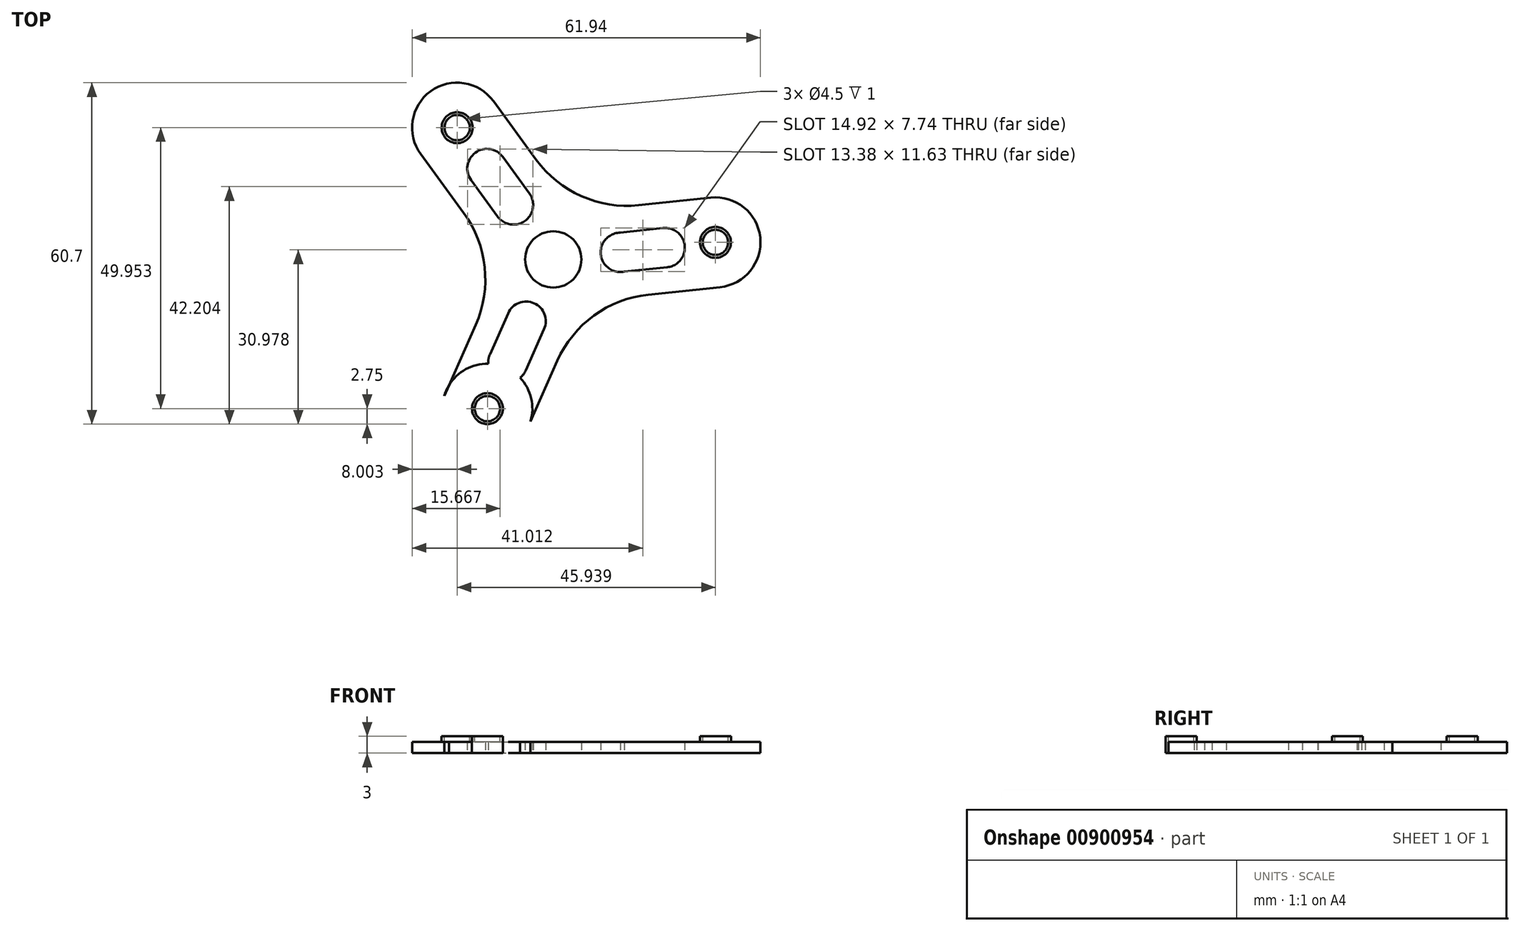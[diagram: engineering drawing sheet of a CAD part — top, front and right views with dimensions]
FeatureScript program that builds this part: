
annotation { "Feature Type Name" : "Feature", "Feature Type Description" : "" }
export const myFeature = defineFeature(function(context is Context, id is Id, definition is map)
    precondition{}
    {
        {
            var Q0;
            Q0=qCreatedBy(makeId("Top.planeOp"),FACE);
            var sketch = newSketch(context, id + "F0", { "sketchPlane" : qUnion([Q0])});
            skCircle(sketch, "E0", {"center": v(0, 0) * mm, "radius": 5 * mm});
            skCircle(sketch, "E1.cCircle", {"center": v(0.02, -0.03) * mm, "radius": 6.16 * mm, "construction": true});
            skLineSegment(sketch, "E1.0", {"start": v(-7.25, 9.93) * mm, "end": v(12.28, 1.29) * mm, "construction": true});
            skLineSegment(sketch, "E1.1", {"start": v(12.28, 1.29) * mm, "end": v(-4.97, -11.3) * mm, "construction": true});
            skLineSegment(sketch, "E1.2", {"start": v(-4.97, -11.3) * mm, "end": v(-7.25, 9.93) * mm, "construction": true});
            skPoint(sketch, "E1.0.midPoint", {"position": v(2.51, 5.61) * mm});
            skLineSegment(sketch, "E2", {"start": v(0, 0) * mm, "end": v(41.18, 4.33) * mm, "construction": true});
            skLineSegment(sketch, "E3", {"start": v(-12.12, -27.46) * mm, "end": v(0.02, -0.03) * mm, "construction": true});
            skLineSegment(sketch, "E4", {"start": v(0, 0) * mm, "end": v(-17.77, 24.35) * mm, "construction": true});
            skCircle(sketch, "E5", {"center": v(28.84, 3.03) * mm, "radius": 8 * mm});
            skCircle(sketch, "E6", {"center": v(-17.1, 23.42) * mm, "radius": 8 * mm});
            skCircle(sketch, "E7", {"center": v(-11.71, -26.53) * mm, "radius": 8 * mm});
            skLineSegment(sketch, "E8", {"start": v(-23.56, 18.7) * mm, "end": v(-10.64, 28.14) * mm, "construction": true});
            skLineSegment(sketch, "E9", {"start": v(28, 10.99) * mm, "end": v(29.68, -4.93) * mm, "construction": true});
            skLineSegment(sketch, "E10", {"start": v(-19.38, -24.25) * mm, "end": v(-4.87, -30.67) * mm, "construction": true});
            skLineSegment(sketch, "E11", {"start": v(-19.38, -24.25) * mm, "end": v(-9.12, -1.07) * mm});
            skLineSegment(sketch, "E12", {"start": v(-23.56, 18.7) * mm, "end": v(-9.12, -1.07) * mm});
            skLineSegment(sketch, "E13", {"start": v(-10.64, 28.14) * mm, "end": v(3.75, 8.44) * mm});
            skLineSegment(sketch, "E14", {"start": v(28, 10.99) * mm, "end": v(3.75, 8.44) * mm});
            skLineSegment(sketch, "E15", {"start": v(29.68, -4.93) * mm, "end": v(5.4, -7.48) * mm});
            skLineSegment(sketch, "E16", {"start": v(-4.87, -30.67) * mm, "end": v(5.4, -7.48) * mm});
            skCircle(sketch, "E17", {"center": v(-17.1, 23.42) * mm, "radius": 2.25 * mm});
            skCircle(sketch, "E18", {"center": v(-17.1, 23.42) * mm, "radius": 2.75 * mm});
            skCircle(sketch, "E19", {"center": v(28.84, 3.03) * mm, "radius": 2.25 * mm});
            skCircle(sketch, "E20", {"center": v(28.84, 3.03) * mm, "radius": 2.75 * mm});
            skCircle(sketch, "E21", {"center": v(-11.71, -26.53) * mm, "radius": 2.25 * mm});
            skCircle(sketch, "E22", {"center": v(-11.71, -26.53) * mm, "radius": 2.75 * mm});
            skCircle(sketch, "E23", {"center": v(-11.8, 16.15) * mm, "radius": 3.5 * mm});
            skCircle(sketch, "E24", {"center": v(-7.07, 9.7) * mm, "radius": 3.5 * mm});
            skCircle(sketch, "E25", {"center": v(11.93, 1.25) * mm, "radius": 3.5 * mm});
            skCircle(sketch, "E26", {"center": v(19.9, 2.09) * mm, "radius": 3.5 * mm});
            skCircle(sketch, "E27", {"center": v(-8.07, -18.3) * mm, "radius": 3.5 * mm});
            skCircle(sketch, "E28", {"center": v(-4.83, -10.98) * mm, "radius": 3.5 * mm});
            skLineSegment(sketch, "E29", {"start": v(11.91, 4.75) * mm, "end": v(12.64, -2.17) * mm, "construction": true});
            skLineSegment(sketch, "E30", {"start": v(19.52, 5.57) * mm, "end": v(20.26, -1.4) * mm, "construction": true});
            skLineSegment(sketch, "E31", {"start": v(19.52, 5.57) * mm, "end": v(11.91, 4.75) * mm});
            skLineSegment(sketch, "E32", {"start": v(12.64, -2.17) * mm, "end": v(20.26, -1.4) * mm});
            skLineSegment(sketch, "E33", {"start": v(-8.03, -9.57) * mm, "end": v(-1.63, -12.4) * mm, "construction": true});
            skLineSegment(sketch, "E34", {"start": v(-11.27, -16.88) * mm, "end": v(-4.87, -19.72) * mm, "construction": true});
            skLineSegment(sketch, "E35", {"start": v(-11.27, -16.88) * mm, "end": v(-8.03, -9.57) * mm});
            skLineSegment(sketch, "E36", {"start": v(-1.63, -12.4) * mm, "end": v(-4.87, -19.72) * mm});
            skLineSegment(sketch, "E37", {"start": v(-14.62, 14.1) * mm, "end": v(-8.96, 18.22) * mm, "construction": true});
            skLineSegment(sketch, "E38", {"start": v(-9.9, 7.63) * mm, "end": v(-4.25, 11.76) * mm, "construction": true});
            skLineSegment(sketch, "E39", {"start": v(-8.96, 18.22) * mm, "end": v(-4.25, 11.76) * mm});
            skLineSegment(sketch, "E40", {"start": v(-9.9, 7.63) * mm, "end": v(-14.62, 14.1) * mm});
            skSolve(sketch);
        }
        {
            var Q0;
            {var subQ0=sQuery(id+"F0.wireOp",EDGE,"E6");var subQ1=makeQuery(id+"F0.imprint","INTERSECT",VERTEX,{"derivedFrom":[subQ0,sQuery(id+"F0.wireOp",EDGE,"E12")]});Q0=makeQuery(id+"F0.imprint","IMPRINT",FACE,{"disambiguationData":[TD([[makeQuery(id+"F0.imprint","IMPRINT",EDGE,{"disambiguationData":[TD([[subQ1,1.0]])],"derivedFrom":subQ0}),1.0]])]});}
            var Q1;
            {var subQ0=sQuery(id+"F0.wireOp",EDGE,"E11");var subQ1=sQuery(id+"F0.wireOp",EDGE,"E7");var subQ2=makeQuery(id+"F0.imprint","INTERSECT",VERTEX,{"disambiguationData":[OD(0.0)],"derivedFrom":[subQ1,subQ0]});Q1=makeQuery(id+"F0.imprint","IMPRINT",FACE,{"disambiguationData":[TD([[makeQuery(id+"F0.imprint","IMPRINT",EDGE,{"disambiguationData":[TD([[subQ2,-1.0]])],"derivedFrom":subQ1}),1.0]])]});}
            var Q2;
            {var subQ0=sQuery(id+"F0.wireOp",EDGE,"E5");var subQ1=makeQuery(id+"F0.imprint","INTERSECT",VERTEX,{"derivedFrom":[subQ0,sQuery(id+"F0.wireOp",EDGE,"E14")]});Q2=makeQuery(id+"F0.imprint","IMPRINT",FACE,{"disambiguationData":[TD([[makeQuery(id+"F0.imprint","IMPRINT",EDGE,{"disambiguationData":[TD([[subQ1,-1.0]])],"derivedFrom":subQ0}),1.0]])]});}
            var Q3;
            Q3=makeQuery(id+"F0.imprint","IMPRINT",FACE,{"disambiguationData":[TD([[makeQuery(id+"F0.imprint","IMPRINT",EDGE,{"derivedFrom":sQuery(id+"F0.wireOp",EDGE,"E0")}),-1.0]])]});
            var Q4;
            Q4=makeQuery(id+"F0.imprint","IMPRINT",FACE,{"disambiguationData":[TD([[makeQuery(id+"F0.imprint","IMPRINT",EDGE,{"derivedFrom":sQuery(id+"F0.wireOp",EDGE,"E17")}),-1.0]])]});
            var Q5;
            Q5=makeQuery(id+"F0.imprint","IMPRINT",FACE,{"disambiguationData":[TD([[makeQuery(id+"F0.imprint","IMPRINT",EDGE,{"derivedFrom":sQuery(id+"F0.wireOp",EDGE,"E17")}),1.0]])]});
            var Q6;
            Q6=makeQuery(id+"F0.imprint","IMPRINT",FACE,{"disambiguationData":[TD([[makeQuery(id+"F0.imprint","IMPRINT",EDGE,{"derivedFrom":sQuery(id+"F0.wireOp",EDGE,"E21")}),1.0]])]});
            var Q7;
            Q7=makeQuery(id+"F0.imprint","IMPRINT",FACE,{"disambiguationData":[TD([[makeQuery(id+"F0.imprint","IMPRINT",EDGE,{"derivedFrom":sQuery(id+"F0.wireOp",EDGE,"E21")}),-1.0]])]});
            var Q8;
            Q8=makeQuery(id+"F0.imprint","IMPRINT",FACE,{"disambiguationData":[TD([[makeQuery(id+"F0.imprint","IMPRINT",EDGE,{"derivedFrom":sQuery(id+"F0.wireOp",EDGE,"E19")}),1.0]])]});
            var Q9;
            Q9=makeQuery(id+"F0.imprint","IMPRINT",FACE,{"disambiguationData":[TD([[makeQuery(id+"F0.imprint","IMPRINT",EDGE,{"derivedFrom":sQuery(id+"F0.wireOp",EDGE,"E19")}),-1.0]])]});
            extrude(context, id + "F1", {"entities" : qUnion([Q0, Q1, Q2, Q3, Q4, Q5, Q6, Q7, Q8, Q9]), "depth" : 2 * mm, "offsetDistance" : 25 * mm});
        }
        {
            var Q0;
            Q0=makeQuery(id+"F0.imprint","IMPRINT",FACE,{"disambiguationData":[TD([[makeQuery(id+"F0.imprint","IMPRINT",EDGE,{"derivedFrom":sQuery(id+"F0.wireOp",EDGE,"E17")}),-1.0]])]});
            var Q1;
            Q1=makeQuery(id+"F0.imprint","IMPRINT",FACE,{"disambiguationData":[TD([[makeQuery(id+"F0.imprint","IMPRINT",EDGE,{"derivedFrom":sQuery(id+"F0.wireOp",EDGE,"E17")}),1.0]])]});
            var Q2;
            Q2=makeQuery(id+"F0.imprint","IMPRINT",FACE,{"disambiguationData":[TD([[makeQuery(id+"F0.imprint","IMPRINT",EDGE,{"derivedFrom":sQuery(id+"F0.wireOp",EDGE,"E19")}),1.0]])]});
            var Q3;
            Q3=makeQuery(id+"F0.imprint","IMPRINT",FACE,{"disambiguationData":[TD([[makeQuery(id+"F0.imprint","IMPRINT",EDGE,{"derivedFrom":sQuery(id+"F0.wireOp",EDGE,"E19")}),-1.0]])]});
            var Q4;
            Q4=makeQuery(id+"F0.imprint","IMPRINT",FACE,{"disambiguationData":[TD([[makeQuery(id+"F0.imprint","IMPRINT",EDGE,{"derivedFrom":sQuery(id+"F0.wireOp",EDGE,"E21")}),1.0]])]});
            var Q5;
            Q5=makeQuery(id+"F0.imprint","IMPRINT",FACE,{"disambiguationData":[TD([[makeQuery(id+"F0.imprint","IMPRINT",EDGE,{"derivedFrom":sQuery(id+"F0.wireOp",EDGE,"E21")}),-1.0]])]});
            extrude(context, id + "F2", {"entities" : qUnion([Q0, Q1, Q2, Q3, Q4, Q5]), "operationType" : NewBodyOperationType.ADD, "depth" : 3 * mm, "offsetDistance" : 25 * mm});
        }
        {
            var Q0;
            Q0=makeQuery(id+"F0.imprint","IMPRINT",FACE,{"disambiguationData":[TD([[makeQuery(id+"F0.imprint","IMPRINT",EDGE,{"derivedFrom":sQuery(id+"F0.wireOp",EDGE,"E21")}),1.0]])]});
            var Q1;
            Q1=makeQuery(id+"F0.imprint","IMPRINT",FACE,{"disambiguationData":[TD([[makeQuery(id+"F0.imprint","IMPRINT",EDGE,{"derivedFrom":sQuery(id+"F0.wireOp",EDGE,"E17")}),1.0]])]});
            var Q2;
            Q2=makeQuery(id+"F0.imprint","IMPRINT",FACE,{"disambiguationData":[TD([[makeQuery(id+"F0.imprint","IMPRINT",EDGE,{"derivedFrom":sQuery(id+"F0.wireOp",EDGE,"E19")}),1.0]])]});
            extrude(context, id + "F3", {"entities" : qUnion([Q0, Q1, Q2]), "operationType" : NewBodyOperationType.ADD, "depth" : 9 * mm, "offsetDistance" : 25 * mm});
        }
        {
            var Q0;
            Q0=makeQuery(id+"F1.opExtrude","SWEPT_EDGE",EDGE,{"disambiguationData":[OSD([sQuery(id+"F0.wireOp",EDGE,"E13"),sQuery(id+"F0.wireOp",EDGE,"E14")])]});
            fillet(context, id + "F4", {"entities" : qUnion([Q0]), "radius" : 20 * mm, "tangentPropagation" : true, "allowEdgeOverflow" : false});
        }
        {
            var Q0;
            Q0=makeQuery(id+"F1.opExtrude","SWEPT_EDGE",EDGE,{"disambiguationData":[OSD([sQuery(id+"F0.wireOp",EDGE,"E11"),sQuery(id+"F0.wireOp",EDGE,"E12")])]});
            fillet(context, id + "F5", {"entities" : qUnion([Q0]), "radius" : 20 * mm, "tangentPropagation" : true, "allowEdgeOverflow" : false});
        }
        {
            var Q0;
            Q0=makeQuery(id+"F1.opExtrude","SWEPT_EDGE",EDGE,{"disambiguationData":[OSD([sQuery(id+"F0.wireOp",EDGE,"E15"),sQuery(id+"F0.wireOp",EDGE,"E16")])]});
            fillet(context, id + "F6", {"entities" : qUnion([Q0]), "radius" : 20 * mm, "tangentPropagation" : true, "allowEdgeOverflow" : false});
        }
        {
            var Q0;
            Q0=makeQuery(id+"F3.opExtrude","CAP_FACE",FACE,{"disambiguationData":[OSD([sQuery(id+"F0.wireOp",EDGE,"E21")])],"isStart":false});
            var Q1;
            Q1=makeQuery(id+"F3.opExtrude","CAP_FACE",FACE,{"disambiguationData":[OSD([sQuery(id+"F0.wireOp",EDGE,"E17")])],"isStart":false});
            var Q2;
            Q2=makeQuery(id+"F3.opExtrude","CAP_FACE",FACE,{"disambiguationData":[OSD([sQuery(id+"F0.wireOp",EDGE,"E19")])],"isStart":false});
            extrude(context, id + "F7", {"entities" : qUnion([Q0, Q1, Q2]), "operationType" : NewBodyOperationType.REMOVE, "oppositeDirection" : true, "depth" : 7 * mm, "offsetDistance" : 25 * mm});
        }
    });
